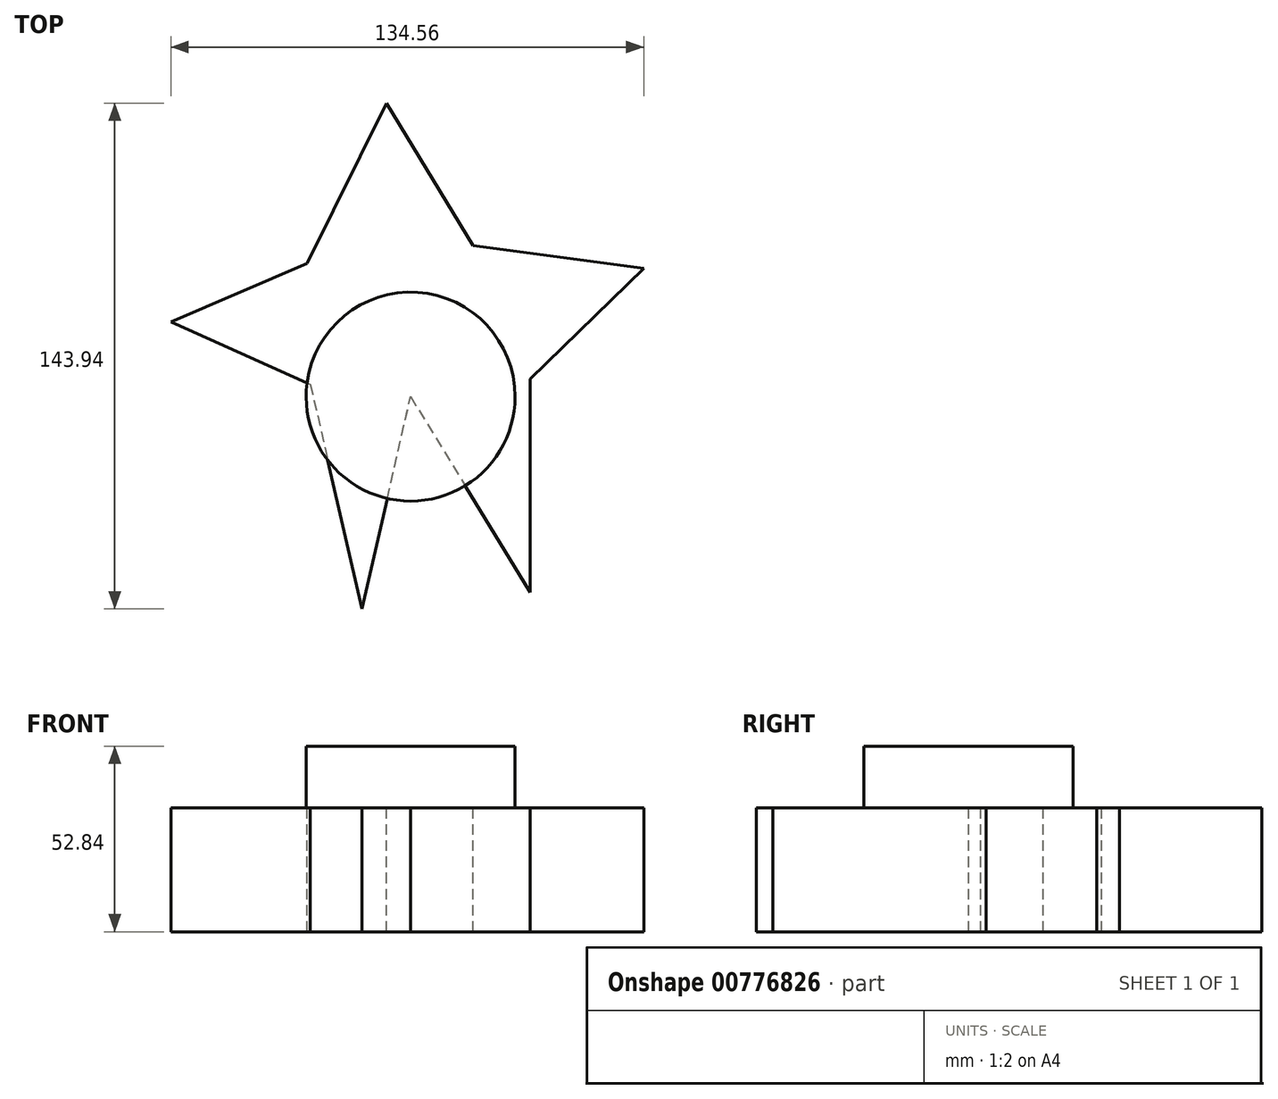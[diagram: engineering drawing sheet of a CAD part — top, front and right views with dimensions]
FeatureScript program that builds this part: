
annotation { "Feature Type Name" : "Feature", "Feature Type Description" : "" }
export const myFeature = defineFeature(function(context is Context, id is Id, definition is map)
    precondition{}
    {
        {
            var Q0;
            Q0=qCreatedBy(makeId("Top.planeOp"),FACE);
            var sketch = newSketch(context, id + "F0", { "sketchPlane" : qUnion([Q0])});
            skLineSegment(sketch, "E0", {"start": v(-29.5, 37.9) * mm, "end": v(-68.21, 21.26) * mm});
            skLineSegment(sketch, "E1", {"start": v(-68.21, 21.26) * mm, "end": v(-28.56, 3.5) * mm});
            skLineSegment(sketch, "E2", {"start": v(-28.56, 3.5) * mm, "end": v(-13.85, -60.45) * mm});
            skLineSegment(sketch, "E3", {"start": v(-13.85, -60.45) * mm, "end": v(0, 0) * mm});
            skLineSegment(sketch, "E4", {"start": v(0, 0) * mm, "end": v(34.04, -55.66) * mm});
            skLineSegment(sketch, "E5", {"start": v(34.04, -55.66) * mm, "end": v(34.04, 5) * mm});
            skLineSegment(sketch, "E6", {"start": v(34.04, 5) * mm, "end": v(66.35, 36.45) * mm});
            skLineSegment(sketch, "E7", {"start": v(66.35, 36.45) * mm, "end": v(17.76, 43) * mm});
            skLineSegment(sketch, "E8", {"start": v(17.76, 43) * mm, "end": v(-6.83, 83.49) * mm});
            skLineSegment(sketch, "E9", {"start": v(-6.83, 83.49) * mm, "end": v(-29.5, 37.9) * mm});
            skSolve(sketch);
        }
        {
            var Q0;
            Q0=makeQuery(id+"F0.imprint","IMPRINT",FACE,{"disambiguationData":[TD([[makeQuery(id+"F0.imprint","IMPRINT",EDGE,{"derivedFrom":sQuery(id+"F0.wireOp",EDGE,"E0")}),1.0]])]});
            extrude(context, id + "F1", {"entities" : qUnion([Q0]), "oppositeDirection" : true, "depth" : 35.3 * mm, "offsetDistance" : 25.4 * mm});
        }
        {
            var Q0;
            Q0=qCreatedBy(makeId("Top.planeOp"),FACE);
            var sketch = newSketch(context, id + "F2", { "sketchPlane" : qUnion([Q0])});
            skCircle(sketch, "E10", {"center": v(0, 0) * mm, "radius": 29.73 * mm});
            skSolve(sketch);
        }
        {
            var Q0;
            Q0 = qSketchRegion(id + "F2", true);
            extrude(context, id + "F3", {"entities" : qUnion([Q0]), "operationType" : NewBodyOperationType.ADD, "depth" : 17.53 * mm, "offsetDistance" : 25.4 * mm});
        }
    });
